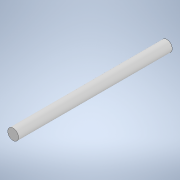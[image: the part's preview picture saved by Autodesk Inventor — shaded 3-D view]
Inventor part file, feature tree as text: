
AUTODESK INVENTOR PART (.ipt)
format: ipt  version: 2021 (Build 250183000, 183)  size: 101,888 bytes
history: native  units: mm
features: extrude x3, sketch x3
ambient origin geometry x8: Origin, YZ Plane, XZ Plane, XY Plane, X Axis, Y Axis, Z Axis, Center Point
bodies: Solid1 (feature_tree)
feature tree (6):
  extrude  "Extrusion1"  Depth=30.0mm TaperAngle=0.0deg
  extrude  "Extrusion3"  Depth=6.0mm TaperAngle=0.0deg
  extrude  "Extrusion4"  Depth=0.872665mm
  sketch  "Sketch1"  dims[d0=3.0mm d1=30.0mm d2=0.0mm]
  sketch  "Sketch4"  dims[d6=6.5mm d7=0.0mm d8=6.0mm d9=0.0mm]
  sketch  "Sketch5"  dims[d4=0.5mm d5=0.872665mm]
